FCSTD DOCUMENT  (FreeCAD 0.18R14555 (Git shallow))
Label: FirstTry
License: All rights reserved
LicenseURL: http://en.wikipedia.org/wiki/All_rights_reserved
objects: Sketcher::SketchObject×1, PartDesign::Body×1, Spreadsheet::Sheet×1
note: 2 computed .brp shape members not serialized (recipe doc carries the construction recipe); baked Part::Feature solids carry a one-line shape summary decoded from their .brp

FEATURE [Sketcher::SketchObject] Sketch
  MapMode = 5
  Support = -> [XY_Plane]
  expr: Constraints[36] = Parameters.WY_1 - Parameters.RW_1 - Parameters.RW_2
  expr: Constraints[27] = Parameters.FW_1
  expr: Constraints[9] = Parameters.KY_6
  expr: Constraints[14] = Parameters.RW_6
  expr: Constraints[16] = Parameters.RW_5
  expr: Constraints[8] = Parameters.KX_6
  expr: Constraints[35] = Parameters.RW_4
  expr: Constraints[31] = 180 - Parameters.KAT
  expr: Constraints[28] = Parameters.RW_6
  expr: Constraints[19] = Parameters.WX_1
  sketch-geometry (14):
    g0: LineSegment StartX=-74.3732 StartY=50.4284 StartZ=0 EndX=105.627 EndY=50.4284 EndZ=0
    g1: LineSegment StartX=105.627 StartY=-115.572 StartZ=0 EndX=-74.3732 EndY=-115.572 EndZ=0
    g2: LineSegment StartX=-74.3732 StartY=50.4284 StartZ=0 EndX=-74.3732 EndY=-115.572 EndZ=0
    g3: LineSegment StartX=105.627 StartY=50.4284 StartZ=0 EndX=105.627 EndY=-115.572 EndZ=0
    g4: LineSegment StartX=-39.7197 StartY=-8.50133 StartZ=0 EndX=-39.7197 EndY=-94.5013 EndZ=0
    g5: LineSegment StartX=-33.926 StartY=28.1126 StartZ=0 EndX=72.074 EndY=28.1126 EndZ=0
    g6: LineSegment StartX=-35.4771 StartY=-98.744 StartZ=0 EndX=70.5229 EndY=-98.744 EndZ=0
    g7: ArcOfCircle CenterX=70.5229 CenterY=-85.744 CenterZ=0 NormalX=0 NormalY=0 NormalZ=1 AngleXU=0 Radius=13 StartAngle=4.71239 EndAngle=6.28319
    g8: ArcOfCircle CenterX=89.5229 CenterY=-85.744 CenterZ=0 NormalX=0 NormalY=0 NormalZ=1 AngleXU=0 Radius=6 StartAngle=1.5708 EndAngle=3.14159
    g9: LineSegment StartX=89.5229 StartY=22.1126 StartZ=0 EndX=89.5229 EndY=-79.744 EndZ=0
    g10: LineSegment StartX=-39.7197 StartY=-94.5013 StartZ=0 EndX=-35.4771 EndY=-98.744 EndZ=0
    g11: ArcOfCircle CenterX=87.4117 CenterY=22.1126 CenterZ=0 NormalX=0 NormalY=0 NormalZ=1 AngleXU=0 Radius=2.11124 StartAngle=3.2196e-08 EndAngle=1.32645
    g12: LineSegment StartX=72.074 StartY=28.1126 StartZ=0 EndX=87.9224 EndY=24.1611 EndZ=0
    g13: Circle CenterX=-53.1313 CenterY=17.5295 CenterZ=0 NormalX=0 NormalY=0 NormalZ=1 AngleXU=0 Radius=9.75219
  constraints (38):
    c: Coincident(g0,g3)
    c: Coincident(g0,g2)
    c: Coincident(g2,g1)
    c: Coincident(g1,g3)
    c: Vertical(g3)
    c: Vertical(g2)
    c: Horizontal(g0)
    c: Horizontal(g1)
    c: DistanceX(g1,g1) = 180
    c: DistanceY(g2,g2) = 166
    c: Vertical(g4)
    c: Horizontal(g5)
    c: Horizontal(g6)
    c: Coincident(g6,g7)
    c: DistanceX(g7,g7) = 13
    c: Coincident(g8,g7)
    c: DistanceY(g8,g8) = 6
    c: Equal(g7,g6)
    c: Vertical(g9)
    c: DistanceX(g6,g6) = 106
    c: Tangent(g7,g6)
    c: Tangent(g7,g8)
    c: Coincident(g8,g9)
    c: Perpendicular(g8,g9)
    c: Coincident(g10,g4)
    c: Coincident(g6,g10)
    c: Angle(g10,g4) = 2.35619
    c: Distance(g6,g4) = 6
    c: Distance(g7,g6) = 13
    c: Coincident(g9,g11)
    c: Coincident(g12,g5)
    c: Angle(g5,g12) = 2.89725
    c: Coincident(g12,g11)
    c: Tangent(g12,g11)
    c: Tangent(g11,g9)
    c: DistanceY(g11,g5) = 6
    c: DistanceY(g4,g4) = 86
    c: DistanceX(g5,g5) = 106
FEATURE [PartDesign::Body] Body
  Group = -> [Sketch]
  Origin = -> Origin
FEATURE [Spreadsheet::Sheet] Spreadsheet  label="Parameters"
  cells = A1=D_1; B1(D_1)=27; A2=KAT; B2(KAT)=14; A3=KAT_2; B3(KAT_2)=28; A4=KPX; B4(KPX)=69; A5=KPY; B5(KPY)=45; A6=D_2; B6(D_2)=39; A7=RKK_1; B7(RKK_1)=6; A8=KOX; B8(KOX)=53; A9=KOY; B9(KOY)=53; A10=WX_1; B10(WX_1)=106; A11=WX_2; B11(WX_2)=136; A12=WY_1; B12(WY_1)=106; A13=RW_1; B13(RW_1)=6; A14=RW_2; B14(RW_2)=14; A15=RW_3; B15(RW_3)=27; A16=RW_4; B16(RW_4)=6; A17=RW_5; B17(RW_5)=6; A18=RW_6; B18(RW_6)=13; A19=FW_1; B19(FW_1)=6; A20=FW_2; B20(FW_2)=5.5; A21=KX_1; B21(KX_1)=12; A22=KX_2; B22(KX_2)=17; A23=KX_3; B23(KX_3)=68; A24=KX_4; B24(KX_4)=139; A25=KX_5; B25(KX_5)=168; A26=KX_6; B26(KX_6)=180; A27=KY_1; B27(KY_1)=12; A28=KY_2; B28(KY_2)=38; A29=KY_3; B29(KY_3)=109; A30=KY_4; B30(KY_4)=146; A31=KY_5; B31(KY_5)=154; A32=KY_6; B32(KY_6)=166; A33=FK_1; B33(FK_1)=2; A34=RK_1; B34(RK_1)=2; A35=H_1; B35(H_1)=12; A36=H_2; B36(H_2)=18; A37=KH_1; B37(KH_1)=10; A38=KH_2; B38(KH_2)=6; A39=OTWX_1; B39(OTWX_1)=9; A40=OTWY_1; B40(OTWY_1)=7; A41=OTWY_2; B41(OTWY_2)=14; A42=GOTW_1; B42(GOTW_1)=14; A43=GOTW_2; B43(GOTW_2)=10
